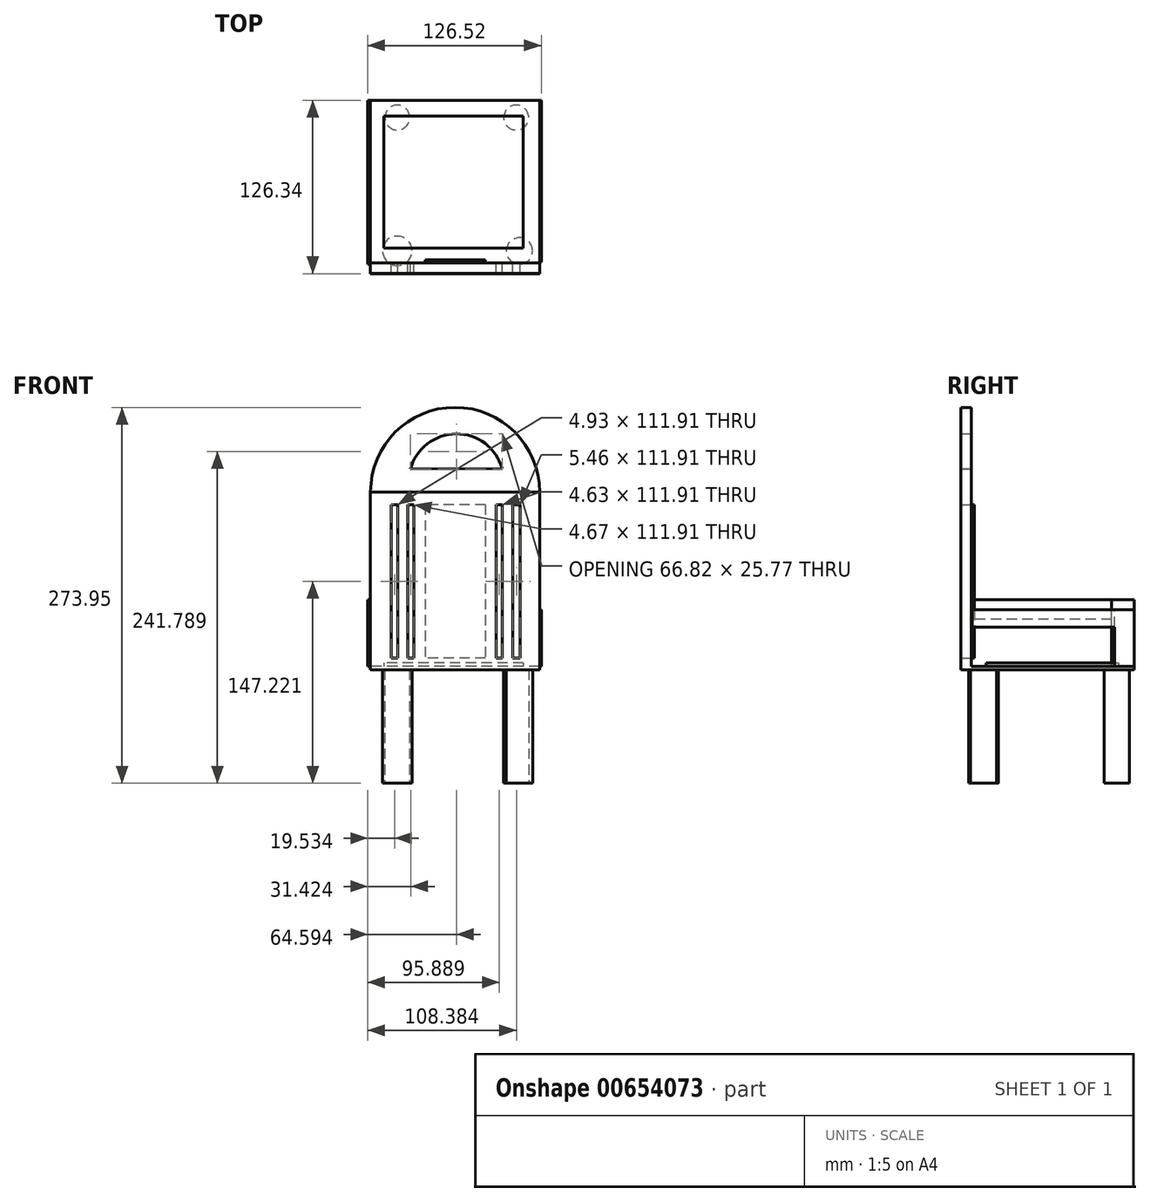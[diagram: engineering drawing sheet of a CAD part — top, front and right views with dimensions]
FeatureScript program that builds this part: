
annotation { "Feature Type Name" : "Feature", "Feature Type Description" : "" }
export const myFeature = defineFeature(function(context is Context, id is Id, definition is map)
    precondition{}
    {
        {
            var Q0;
            Q0=qCreatedBy(makeId("Top.planeOp"),FACE);
            var sketch = newSketch(context, id + "F0", { "sketchPlane" : qUnion([Q0])});
            skCircle(sketch, "E0", {"center": v(-39.87, 52.11) * mm, "radius": 9.06 * mm});
            skCircle(sketch, "E1", {"center": v(-39.87, -45.02) * mm, "radius": 10.72 * mm});
            skCircle(sketch, "E2", {"center": v(49.2, -45.02) * mm, "radius": 9.57 * mm});
            skCircle(sketch, "E3", {"center": v(46.84, 52.11) * mm, "radius": 9.11 * mm});
            skSolve(sketch);
        }
        {
            var Q0;
            Q0 = qSketchRegion(id + "F0", true);
            extrude(context, id + "F1", {"entities" : qUnion([Q0]), "depth" : 82.8 * mm, "offsetDistance" : 25.4 * mm});
        }
        {
            var Q0;
            Q0=qCreatedBy(makeId("Top.planeOp"),FACE);
            var sketch = newSketch(context, id + "F2", { "sketchPlane" : qUnion([Q0])});
            skLineSegment(sketch, "E4.bottom", {"start": v(12.26, 295.73) * mm, "end": v(123.67, 295.73) * mm});
            skLineSegment(sketch, "E4.top", {"start": v(12.26, 100.5) * mm, "end": v(123.67, 100.5) * mm});
            skLineSegment(sketch, "E4.left", {"start": v(12.26, 295.73) * mm, "end": v(12.26, 100.5) * mm});
            skLineSegment(sketch, "E4.right", {"start": v(123.67, 295.73) * mm, "end": v(123.67, 100.5) * mm});
            skSolve(sketch);
        }
        {
            var Q0;
            Q0 = qSketchRegion(id + "F2", true);
            extrude(context, id + "F3", {"entities" : qUnion([Q0]), "depth" : 3.56 * mm, "offsetDistance" : 25.4 * mm});
        }
        {
            var Q0;
            Q0=makeQuery(id+"F3.opExtrude","SWEPT_BODY",BODY,{"disambiguationData":[OSD([sQuery(id+"F2.wireOp",EDGE,"E4.bottom"),sQuery(id+"F2.wireOp",EDGE,"E4.top"),sQuery(id+"F2.wireOp",EDGE,"E4.left"),sQuery(id+"F2.wireOp",EDGE,"E4.right")])]});
            deleteBodies(context, id + "F4", {"entities" : qUnion([Q0])});
        }
        {
            var Q0;
            Q0=qCreatedBy(makeId("Top.planeOp"),FACE);
            var sketch = newSketch(context, id + "F5", { "sketchPlane" : qUnion([Q0])});
            skLineSegment(sketch, "E5.bottom", {"start": v(106.89, 141.66) * mm, "end": v(197.05, 141.66) * mm});
            skLineSegment(sketch, "E5.top", {"start": v(106.89, 0) * mm, "end": v(197.05, 0) * mm});
            skLineSegment(sketch, "E5.left", {"start": v(106.89, 141.66) * mm, "end": v(106.89, 0) * mm});
            skLineSegment(sketch, "E5.right", {"start": v(197.05, 141.66) * mm, "end": v(197.05, 0) * mm});
            skSolve(sketch);
        }
        {
            var Q0;
            Q0 = qSketchRegion(id + "F5", true);
            extrude(context, id + "F6", {"entities" : qUnion([Q0]), "depth" : 2.03 * mm, "offsetDistance" : 25.4 * mm});
        }
        {
            var Q0;
            Q0=makeQuery(id+"F6.opExtrude","SWEPT_BODY",BODY,{"disambiguationData":[OSD([sQuery(id+"F5.wireOp",EDGE,"E5.bottom"),sQuery(id+"F5.wireOp",EDGE,"E5.top"),sQuery(id+"F5.wireOp",EDGE,"E5.left"),sQuery(id+"F5.wireOp",EDGE,"E5.right")])]});
            deleteBodies(context, id + "F7", {"entities" : qUnion([Q0])});
        }
        {
            var Q0;
            Q0=makeQuery(id+"F1.opExtrude","CAP_FACE",FACE,{"disambiguationData":[OSD([sQuery(id+"F0.wireOp",EDGE,"E1")])],"isStart":false});
            var sketch = newSketch(context, id + "F8", { "sketchPlane" : qUnion([Q0])});
            skLineSegment(sketch, "E6.bottom", {"start": v(-59.37, -61.59) * mm, "end": v(63.85, -61.59) * mm});
            skLineSegment(sketch, "E6.top", {"start": v(-59.37, 64.75) * mm, "end": v(63.85, 64.75) * mm});
            skLineSegment(sketch, "E6.left", {"start": v(-59.37, -61.59) * mm, "end": v(-59.37, 64.75) * mm});
            skLineSegment(sketch, "E6.right", {"start": v(63.85, -61.59) * mm, "end": v(63.85, 64.75) * mm});
            skSolve(sketch);
        }
        {
            var Q0;
            Q0 = qSketchRegion(id + "F8", true);
            extrude(context, id + "F9", {"entities" : qUnion([Q0]), "depth" : 2.54 * mm, "offsetDistance" : 25.4 * mm});
        }
        {
            var Q0;
            Q0=makeQuery(id+"F9.opExtrude","CAP_FACE",FACE,{"disambiguationData":[OSD([sQuery(id+"F8.wireOp",EDGE,"E6.bottom"),sQuery(id+"F8.wireOp",EDGE,"E6.top"),sQuery(id+"F8.wireOp",EDGE,"E6.left"),sQuery(id+"F8.wireOp",EDGE,"E6.right")])],"isStart":false});
            var sketch = newSketch(context, id + "F10", { "sketchPlane" : qUnion([Q0])});
            skLineSegment(sketch, "E7.bottom", {"start": v(63.85, -53.87) * mm, "end": v(-59.37, -53.87) * mm});
            skLineSegment(sketch, "E7.top", {"start": v(63.85, -61.59) * mm, "end": v(-59.37, -61.59) * mm});
            skLineSegment(sketch, "E7.left", {"start": v(63.85, -53.87) * mm, "end": v(63.85, -61.59) * mm});
            skLineSegment(sketch, "E7.right", {"start": v(-59.37, -53.87) * mm, "end": v(-59.37, -61.59) * mm});
            skSolve(sketch);
        }
        {
            var Q0;
            Q0 = qSketchRegion(id + "F10", true);
            extrude(context, id + "F11", {"entities" : qUnion([Q0]), "operationType" : NewBodyOperationType.ADD, "depth" : 127 * mm, "offsetDistance" : 25.4 * mm});
        }
        {
            var Q0;
            Q0=makeQuery(id+"F11.opExtrude","SWEPT_FACE",FACE,{"disambiguationData":[OSD([sQuery(id+"F10.wireOp",EDGE,"E7.bottom")])]});
            var sketch = newSketch(context, id + "F12", { "sketchPlane" : qUnion([Q0])});
            skLineSegment(sketch, "E8.bottom", {"start": v(-49.71, 203.18) * mm, "end": v(-44.25, 203.18) * mm});
            skLineSegment(sketch, "E8.top", {"start": v(-49.71, 91.26) * mm, "end": v(-44.25, 91.26) * mm});
            skLineSegment(sketch, "E8.left", {"start": v(-49.71, 203.18) * mm, "end": v(-49.71, 91.26) * mm});
            skLineSegment(sketch, "E8.right", {"start": v(-44.25, 203.18) * mm, "end": v(-44.25, 91.26) * mm});
            skSolve(sketch);
        }
        {
            var Q0;
            Q0 = qSketchRegion(id + "F12", true);
            extrude(context, id + "F13", {"entities" : qUnion([Q0]), "operationType" : NewBodyOperationType.REMOVE, "oppositeDirection" : true, "depth" : 25.4 * mm, "offsetDistance" : 25.4 * mm});
        }
        {
            var Q0;
            Q0=makeQuery(id+"F11.opExtrude","SWEPT_FACE",FACE,{"disambiguationData":[OSD([sQuery(id+"F10.wireOp",EDGE,"E7.bottom")])]});
            var sketch = newSketch(context, id + "F14", { "sketchPlane" : qUnion([Q0])});
            skLineSegment(sketch, "E9.bottom", {"start": v(-36.8, 91.26) * mm, "end": v(-32.17, 91.26) * mm});
            skLineSegment(sketch, "E9.top", {"start": v(-36.8, 203.18) * mm, "end": v(-32.17, 203.18) * mm});
            skLineSegment(sketch, "E9.left", {"start": v(-36.8, 91.26) * mm, "end": v(-36.8, 203.18) * mm});
            skLineSegment(sketch, "E9.right", {"start": v(-32.17, 91.26) * mm, "end": v(-32.17, 203.18) * mm});
            skSolve(sketch);
        }
        {
            var Q0;
            Q0 = qSketchRegion(id + "F14", true);
            extrude(context, id + "F15", {"entities" : qUnion([Q0]), "operationType" : NewBodyOperationType.REMOVE, "oppositeDirection" : true, "depth" : 25.4 * mm, "offsetDistance" : 25.4 * mm});
        }
        {
            var Q0;
            Q0=makeQuery(id+"F11.opExtrude","SWEPT_FACE",FACE,{"disambiguationData":[OSD([sQuery(id+"F10.wireOp",EDGE,"E7.bottom")])]});
            var sketch = newSketch(context, id + "F16", { "sketchPlane" : qUnion([Q0])});
            skLineSegment(sketch, "E10.bottom", {"start": v(44.33, 203.18) * mm, "end": v(39.4, 203.18) * mm});
            skLineSegment(sketch, "E10.top", {"start": v(44.33, 91.26) * mm, "end": v(39.4, 91.26) * mm});
            skLineSegment(sketch, "E10.left", {"start": v(44.33, 203.18) * mm, "end": v(44.33, 91.26) * mm});
            skLineSegment(sketch, "E10.right", {"start": v(39.4, 203.18) * mm, "end": v(39.4, 91.26) * mm});
            skSolve(sketch);
        }
        {
            var Q0;
            Q0 = qSketchRegion(id + "F16", true);
            extrude(context, id + "F17", {"entities" : qUnion([Q0]), "operationType" : NewBodyOperationType.REMOVE, "oppositeDirection" : true, "depth" : 25.4 * mm, "offsetDistance" : 25.4 * mm});
        }
        {
            var Q0;
            Q0=makeQuery(id+"F11.opExtrude","SWEPT_FACE",FACE,{"disambiguationData":[OSD([sQuery(id+"F10.wireOp",EDGE,"E7.bottom")])]});
            var sketch = newSketch(context, id + "F18", { "sketchPlane" : qUnion([Q0])});
            skLineSegment(sketch, "E11.bottom", {"start": v(32.31, 203.18) * mm, "end": v(27.64, 203.18) * mm});
            skLineSegment(sketch, "E11.top", {"start": v(32.31, 91.26) * mm, "end": v(27.64, 91.26) * mm});
            skLineSegment(sketch, "E11.left", {"start": v(32.31, 203.18) * mm, "end": v(32.31, 91.26) * mm});
            skLineSegment(sketch, "E11.right", {"start": v(27.64, 203.18) * mm, "end": v(27.64, 91.26) * mm});
            skSolve(sketch);
        }
        {
            var Q0;
            Q0 = qSketchRegion(id + "F18", true);
            extrude(context, id + "F19", {"entities" : qUnion([Q0]), "operationType" : NewBodyOperationType.REMOVE, "oppositeDirection" : true, "depth" : 25.4 * mm, "offsetDistance" : 25.4 * mm});
        }
        {
            var Q0;
            Q0=makeQuery(id+"F11.boolean.opBoolean","MERGE",FACE,{"derivedFrom":[makeQuery(id+"F9.opExtrude","SWEPT_FACE",FACE,{"disambiguationData":[OSD([sQuery(id+"F8.wireOp",EDGE,"E6.right")])]}),makeQuery(id+"F11.opExtrude","SWEPT_FACE",FACE,{"disambiguationData":[OSD([sQuery(id+"F10.wireOp",EDGE,"E7.left")])]})]});
            var sketch = newSketch(context, id + "F20", { "sketchPlane" : qUnion([Q0])});
            skLineSegment(sketch, "E12.bottom", {"start": v(64.75, 85.34) * mm, "end": v(50.43, 85.34) * mm});
            skLineSegment(sketch, "E12.top", {"start": v(64.75, 126.42) * mm, "end": v(50.43, 126.42) * mm});
            skLineSegment(sketch, "E12.left", {"start": v(64.75, 85.34) * mm, "end": v(64.75, 126.42) * mm});
            skLineSegment(sketch, "E12.right", {"start": v(50.43, 85.34) * mm, "end": v(50.43, 126.42) * mm});
            skSolve(sketch);
        }
        {
            var Q0;
            Q0 = qSketchRegion(id + "F20", true);
            extrude(context, id + "F21", {"entities" : qUnion([Q0]), "depth" : 1.27 * mm, "offsetDistance" : 25.4 * mm});
        }
        {
            var Q0;
            Q0=makeQuery(id+"F21.opExtrude","CAP_FACE",FACE,{"disambiguationData":[OSD([sQuery(id+"F20.wireOp",EDGE,"E12.bottom"),sQuery(id+"F20.wireOp",EDGE,"E12.top"),sQuery(id+"F20.wireOp",EDGE,"E12.left"),sQuery(id+"F20.wireOp",EDGE,"E12.right")])],"isStart":false});
            var sketch = newSketch(context, id + "F22", { "sketchPlane" : qUnion([Q0])});
            skLineSegment(sketch, "E13.bottom", {"start": v(50.43, 126.42) * mm, "end": v(-53.3, 126.42) * mm});
            skLineSegment(sketch, "E13.top", {"start": v(50.43, 113.77) * mm, "end": v(-53.3, 113.77) * mm});
            skLineSegment(sketch, "E13.left", {"start": v(50.43, 126.42) * mm, "end": v(50.43, 113.77) * mm});
            skLineSegment(sketch, "E13.right", {"start": v(-53.3, 126.42) * mm, "end": v(-53.3, 113.77) * mm});
            skSolve(sketch);
        }
        {
            var Q0;
            Q0 = qSketchRegion(id + "F22", true);
            extrude(context, id + "F23", {"entities" : qUnion([Q0]), "operationType" : NewBodyOperationType.ADD, "oppositeDirection" : true, "depth" : 0.76 * mm, "offsetDistance" : 25.4 * mm});
        }
        {
            var Q0;
            Q0=makeQuery(id+"F11.boolean.opBoolean","MERGE",FACE,{"derivedFrom":[makeQuery(id+"F9.opExtrude","SWEPT_FACE",FACE,{"disambiguationData":[OSD([sQuery(id+"F8.wireOp",EDGE,"E6.left")])]}),makeQuery(id+"F11.opExtrude","SWEPT_FACE",FACE,{"disambiguationData":[OSD([sQuery(id+"F10.wireOp",EDGE,"E7.right")])]})]});
            var sketch = newSketch(context, id + "F24", { "sketchPlane" : qUnion([Q0])});
            skLineSegment(sketch, "E14.bottom", {"start": v(-64.75, 85.34) * mm, "end": v(-48.4, 85.34) * mm});
            skLineSegment(sketch, "E14.top", {"start": v(-64.75, 133.77) * mm, "end": v(-48.4, 133.77) * mm});
            skLineSegment(sketch, "E14.left", {"start": v(-64.75, 85.34) * mm, "end": v(-64.75, 133.77) * mm});
            skLineSegment(sketch, "E14.right", {"start": v(-48.4, 85.34) * mm, "end": v(-48.4, 133.77) * mm});
            skSolve(sketch);
        }
        {
            var Q0;
            Q0 = qSketchRegion(id + "F24", true);
            extrude(context, id + "F25", {"entities" : qUnion([Q0]), "depth" : 2.03 * mm, "offsetDistance" : 25.4 * mm});
        }
        {
            var Q0;
            Q0=makeQuery(id+"F25.opExtrude","CAP_FACE",FACE,{"disambiguationData":[OSD([sQuery(id+"F24.wireOp",EDGE,"E14.bottom"),sQuery(id+"F24.wireOp",EDGE,"E14.top"),sQuery(id+"F24.wireOp",EDGE,"E14.left"),sQuery(id+"F24.wireOp",EDGE,"E14.right")])],"isStart":false});
            var sketch = newSketch(context, id + "F26", { "sketchPlane" : qUnion([Q0])});
            skLineSegment(sketch, "E15.bottom", {"start": v(-48.4, 133.77) * mm, "end": v(54.63, 133.77) * mm});
            skLineSegment(sketch, "E15.top", {"start": v(-48.4, 119.58) * mm, "end": v(54.63, 119.58) * mm});
            skLineSegment(sketch, "E15.left", {"start": v(-48.4, 133.77) * mm, "end": v(-48.4, 119.58) * mm});
            skLineSegment(sketch, "E15.right", {"start": v(54.63, 133.77) * mm, "end": v(54.63, 119.58) * mm});
            skSolve(sketch);
        }
        {
            var Q0;
            Q0 = qSketchRegion(id + "F26", true);
            extrude(context, id + "F27", {"entities" : qUnion([Q0]), "oppositeDirection" : true, "depth" : 2.03 * mm, "offsetDistance" : 25.4 * mm});
        }
        {
            var Q0;
            Q0=makeQuery(id+"F11.opExtrude","SWEPT_FACE",FACE,{"disambiguationData":[OSD([sQuery(id+"F10.wireOp",EDGE,"E7.bottom")])]});
            var sketch = newSketch(context, id + "F28", { "sketchPlane" : qUnion([Q0])});
            skArc(sketch, "E16", {"start": v(59.37, 212.34) * mm, "mid": v(-2.24, 273.95) * mm, "end": v(-63.85, 212.34) * mm});
            skSolve(sketch);
        }
        {
            var Q0;
            Q0 = qSketchRegion(id + "F28", true);
            var Q1;
            Q1=makeQuery(id+"F28.imprint","IMPRINT",FACE,{"disambiguationData":[TD([[makeQuery(id+"F28.imprint","IMPRINT",EDGE,{"derivedFrom":sQuery(id+"F28.wireOp",EDGE,"E16")}),1.0]])]});
            extrude(context, id + "F29", {"entities" : qUnion([Q0, Q1]), "operationType" : NewBodyOperationType.ADD, "oppositeDirection" : true, "depth" : 7.62 * mm, "offsetDistance" : 25.4 * mm});
        }
        {
            var Q0;
            {var subQ0=sQuery(id+"F10.wireOp",EDGE,"E7.bottom");Q0=makeQuery(id+"F29.boolean.opBoolean","MERGE",FACE,{"derivedFrom":[makeQuery(id+"F11.opExtrude","SWEPT_FACE",FACE,{"disambiguationData":[OSD([subQ0])]}),makeQuery(id+"F29.opExtrude","CAP_FACE",FACE,{"disambiguationData":[OSD([subQ0,sQuery(id+"F28.wireOp",EDGE,"E16")])],"isStart":true})]});}
            var sketch = newSketch(context, id + "F30", { "sketchPlane" : qUnion([Q0])});
            skArc(sketch, "E17", {"start": v(30.21, 228.9) * mm, "mid": v(-3.05, 254.67) * mm, "end": v(-36.6, 229.27) * mm});
            skLineSegment(sketch, "E18", {"start": v(-36.6, 229.27) * mm, "end": v(30.21, 228.9) * mm});
            skSolve(sketch);
        }
        {
            var Q0;
            Q0=makeQuery(id+"F30.imprint","IMPRINT",FACE,{"disambiguationData":[TD([[makeQuery(id+"F30.imprint","IMPRINT",EDGE,{"derivedFrom":sQuery(id+"F30.wireOp",EDGE,"E17")}),1.0]])]});
            extrude(context, id + "F31", {"entities" : qUnion([Q0]), "operationType" : NewBodyOperationType.REMOVE, "oppositeDirection" : true, "depth" : 25.4 * mm, "offsetDistance" : 25.4 * mm});
        }
        {
            var Q0;
            Q0=makeQuery(id+"F9.opExtrude","CAP_FACE",FACE,{"disambiguationData":[OSD([sQuery(id+"F8.wireOp",EDGE,"E6.bottom"),sQuery(id+"F8.wireOp",EDGE,"E6.top"),sQuery(id+"F8.wireOp",EDGE,"E6.left"),sQuery(id+"F8.wireOp",EDGE,"E6.right")])],"isStart":false});
            var sketch = newSketch(context, id + "F32", { "sketchPlane" : qUnion([Q0])});
            skLineSegment(sketch, "E19.bottom", {"start": v(52.02, -42.93) * mm, "end": v(-49.67, -42.93) * mm});
            skLineSegment(sketch, "E19.top", {"start": v(52.02, 53.28) * mm, "end": v(-49.67, 53.28) * mm});
            skLineSegment(sketch, "E19.left", {"start": v(52.02, -42.93) * mm, "end": v(52.02, 53.28) * mm});
            skLineSegment(sketch, "E19.right", {"start": v(-49.67, -42.93) * mm, "end": v(-49.67, 53.28) * mm});
            skSolve(sketch);
        }
        {
            var Q0;
            Q0 = qSketchRegion(id + "F32", true);
            extrude(context, id + "F33", {"entities" : qUnion([Q0]), "operationType" : NewBodyOperationType.ADD, "depth" : 2.3 * mm, "offsetDistance" : 25.4 * mm});
        }
        {
            var Q0;
            {var subQ0=sQuery(id+"F10.wireOp",EDGE,"E7.bottom");Q0=makeQuery(id+"F29.boolean.opBoolean","MERGE",FACE,{"derivedFrom":[makeQuery(id+"F11.opExtrude","SWEPT_FACE",FACE,{"disambiguationData":[OSD([subQ0])]}),makeQuery(id+"F29.opExtrude","CAP_FACE",FACE,{"disambiguationData":[OSD([subQ0,sQuery(id+"F28.wireOp",EDGE,"E16")])],"isStart":true})]});}
            var sketch = newSketch(context, id + "F34", { "sketchPlane" : qUnion([Q0])});
            skLineSegment(sketch, "E20.bottom", {"start": v(-24.43, 203.18) * mm, "end": v(19.53, 203.18) * mm});
            skLineSegment(sketch, "E20.top", {"start": v(-24.43, 91.26) * mm, "end": v(19.53, 91.26) * mm});
            skLineSegment(sketch, "E20.left", {"start": v(-24.43, 203.18) * mm, "end": v(-24.43, 91.26) * mm});
            skLineSegment(sketch, "E20.right", {"start": v(19.53, 203.18) * mm, "end": v(19.53, 91.26) * mm});
            skSolve(sketch);
        }
        {
            var Q0;
            Q0 = qSketchRegion(id + "F34", true);
            extrude(context, id + "F35", {"entities" : qUnion([Q0]), "operationType" : NewBodyOperationType.ADD, "depth" : 2.3 * mm, "offsetDistance" : 25.4 * mm});
        }
    });
